# Revit family: LWplc_Latchwaysplc_FallArrestSystemGuidedAnchorLine_SinglePlyMembraneType2
name_source: partatom
category: Generic Models
revit_build: Autodesk Revit 2014 (Build: 20130709_2115(x64)
units: mm (PartAtom-declared; Revit-internal decimal feet)

## types (4) — shared parameters
AssetType = Fixed
AttachmentDeviceGuide = www.latchways.com/BIM/Latchways_Attachment_Device_Guide.pdf
Color = Dome: Stainless Steel, Electro Polished
Default Elevation = 1219 mm
Depth = 532 mm
Description = Latchways ManSafe® for Single Ply Roofing, using Constant Force posts
DomeLevel = 145 mm
DurationUnit = year
FireExit = No
FixingDetail = www.latchways.com/BIM/Latchways_CFP_SinglePly_FixingDetail.pdf
Height = 208 mm
IfcExportAs = NOTDEFINED
IfcExportType = IfcTransportElement
Length = 532 mm
ManSafeForRoofingBrochure = www.latchways.com/BIM/ManSafeForRoofing.pdf
ManufacturerName = Latchways plc
ManufacturerURL = www.latchways.com
NBSDescription = Fall arrest system - guided anchor line
NBSReference = 80-50-25/110
NominalHeight = 208 mm
NominalLength = 532 mm
NominalWidth = 375 mm
PreInstallationSurvey = Required
ProductSpecification = www.latchways.com/BIM/Latchways_CFP_SinglePly_NBS_Specifications.doc
SystemMaintenance = Annual service to be completed by Latchways registered installers in accordance with BS7883:2005
SystemManufacturer = Latchways plc
URL = www.latchways.com
Uniclass2 = 80-30-25/135
Version = 1
WarrantyDurationUnit = year
Width = 375 mm

## per-type parameters (varying)
| type | BIMObjectName | Material | Model | ModelNumber | ModelReference | Name | ProductInformation | Size | cap_value | weather_cap_on/off |
| CFP for PVC Membranes | LWplc_Latchwaysplc_FallArrestSystemGuidedAnchorLine_SinglePlyMembraneType_Bituminous | Dome: 316s Stainless Steel; Base Plate: Aluminium, Powder Coat | 65619-00 | 65619-00 | Constant Force Post for Bituminous Membranes | FallArrestSystemGuidedAnchorLine_SinglePlyMembraneType_Bituminous_Latchwaysplc | www.latchways.com/BIM/65619-00_LatchwaysConstantForcePost_BituminousRoofing.pdf | 532 x 375 x 197 mm | 0 | No |
| CFP for Bituminous Membranes | LWplc_Latchwaysplc_FallArrestSystemGuidedAnchorLine_SinglePlyMembraneType_Bituminous | Dome: 316s Stainless Steel; Base Plate: Aluminium, Powder Coat | 65619-00 | 65619-00 | Constant Force Post for Bituminous Membranes | FallArrestSystemGuidedAnchorLine_SinglePlyMembraneType_Bituminous_Latchwaysplc | www.latchways.com/BIM/65619-00_LatchwaysConstantForcePost_BituminousRoofing.pdf | 532 x 375 x 197 mm | 0 | No |
| CFP with Weathering Cap - Non PVC | LWplc_Latchwaysplc_FallArrestSystemGuidedAnchorLine_SinglePlyMembraneType_WeatherCap | Dome: 316s Stainless Steel; Base Plate: Aluminium, Powder Coat; Cap: ASA Resin (Natural UV Stabilised) | 65662-00 | 65662-00 | Constant Force Post with Weathering Cap | FallArrestSystemGuidedAnchorLine_SinglePlyMembraneType_WeatherCap_Latchwaysplc | www.latchways.com/BIM/65662-00_LatchwaysConstantForcePost_WeatheringCap-NonPVC.pdf | 532 x 375 x 208 mm | 1 | Yes |
| CFP for EPDM Membranes | LWplc_Latchwaysplc_FallArrestSystemGuidedAnchorLine_SinglePlyMembraneType_EPDM | Dome: 316s Stainless Steel; Base Plate: Aluminium, Powder Coat | 65656-00 | 65656-00 | Constant Force Post for EPDM Membranes | FallArrestSystemGuidedAnchorLine_SinglePlyMembraneType_EPDM_Latchwaysplc | www.latchways.com/BIM/65656-00_LatchwaysConstantForcePost_EPDM-Membrane.pdf | 532 x 375 x 197 mm | 1 | Yes |

## geometry (parser evidence)
native form markers: Sweep x5
no freeform markers — native parametric forms only
